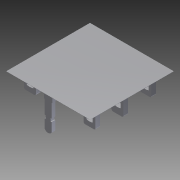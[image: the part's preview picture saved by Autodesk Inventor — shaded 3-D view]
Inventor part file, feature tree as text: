
AUTODESK INVENTOR PART (.ipt)
format: ipt  version: 2011 SP1 (Build 150282100, 282)  size: 196,608 bytes
history: native  units: in
note: dims shown in document units (in); Inventor stores cm internally (conversion verified against a paired STEP export)
features: extrude x9, sketch x9, other x7
ambient origin geometry x8: Origin, YZ Plane, XZ Plane, XY Plane, X Axis, Y Axis, Z Axis, Center Point
bodies: Solid1 (feature_tree)
feature tree (25):
  extrude  "Extrusion1"  Depth=0.024in TaperAngle=0.0deg
  extrude  "Extrusion2"  Depth=0.031in TaperAngle=0.0deg
  extrude  "Extrusion3"  Depth=0.031in TaperAngle=0.0deg
  extrude  "Extrusion4"  Depth=0.031in TaperAngle=0.0deg
  extrude  "Extrusion5"  [1 undecoded]
  extrude  "Extrusion6"  [1 undecoded]
  extrude  "Extrusion7"  [1 undecoded]
  extrude  "Extrusion8"  [1 undecoded]
  extrude  "Extrusion9"  [1 undecoded]
  other  "pins_to_body_XY"
  other  "pins_to_body_YZ"
  other  "pins_to_body_ZX"
  other  "pins_to_body_X"
  other  "pins_to_body_Y"
  other  "pins_to_body_Z"
  other  "pins_to_body_Center"
  sketch  "Sketch_1"  dims[d0=0.001in d1=0.0in d2=0.024in d3=0.0in]
  sketch  "Sketch_3"  dims[d4=0.031in d5=0.0in d6=0.031in d7=0.0in]
  sketch  "Sketch_5"  dims[d12=0.031in d13=0.0in d14=0.031in d15=0.0in]
  sketch  "Sketch_6"  dims[d16=0.024in d17=0.0in]
  sketch  "Sketch_7"
  sketch  "Sketch_8"
  sketch  "Sketch_9"
  sketch  "Sketch_10"
  sketch  "Sketch_4"  dims[d8=0.031in d9=0.0in d10=0.031in d11=0.0in]
note: 5 required parameter values undecoded (feature->parameter linkage not recoverable at this tier; creation-order binding heuristic only, values carry confidence <= 0.55)
